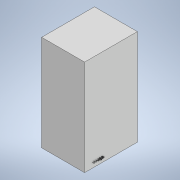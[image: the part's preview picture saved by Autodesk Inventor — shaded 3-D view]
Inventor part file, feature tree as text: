
AUTODESK INVENTOR PART (.ipt)
format: ipt  version: 2021.2 (Build 252289000, 289)  size: 217,600 bytes
history: native  units: in
note: dims shown in document units (in); Inventor stores cm internally (conversion verified against a paired STEP export)
features: sketch x2, extrude x1, emboss x1
ambient origin geometry x8: Origin, YZ Plane, XZ Plane, XY Plane, X Axis, Y Axis, Z Axis, Center Point
bodies: Solid1 (feature_tree)
feature tree (4):
  extrude  "Extrusion1"  Depth=0.01in TaperAngle=0.0deg
  emboss  "Emboss1"
  sketch  "Sketch1"  dims[d0=1.0in d1=0.0in d2=0.01in d3=0.0in]
  sketch  "Sketch2"
